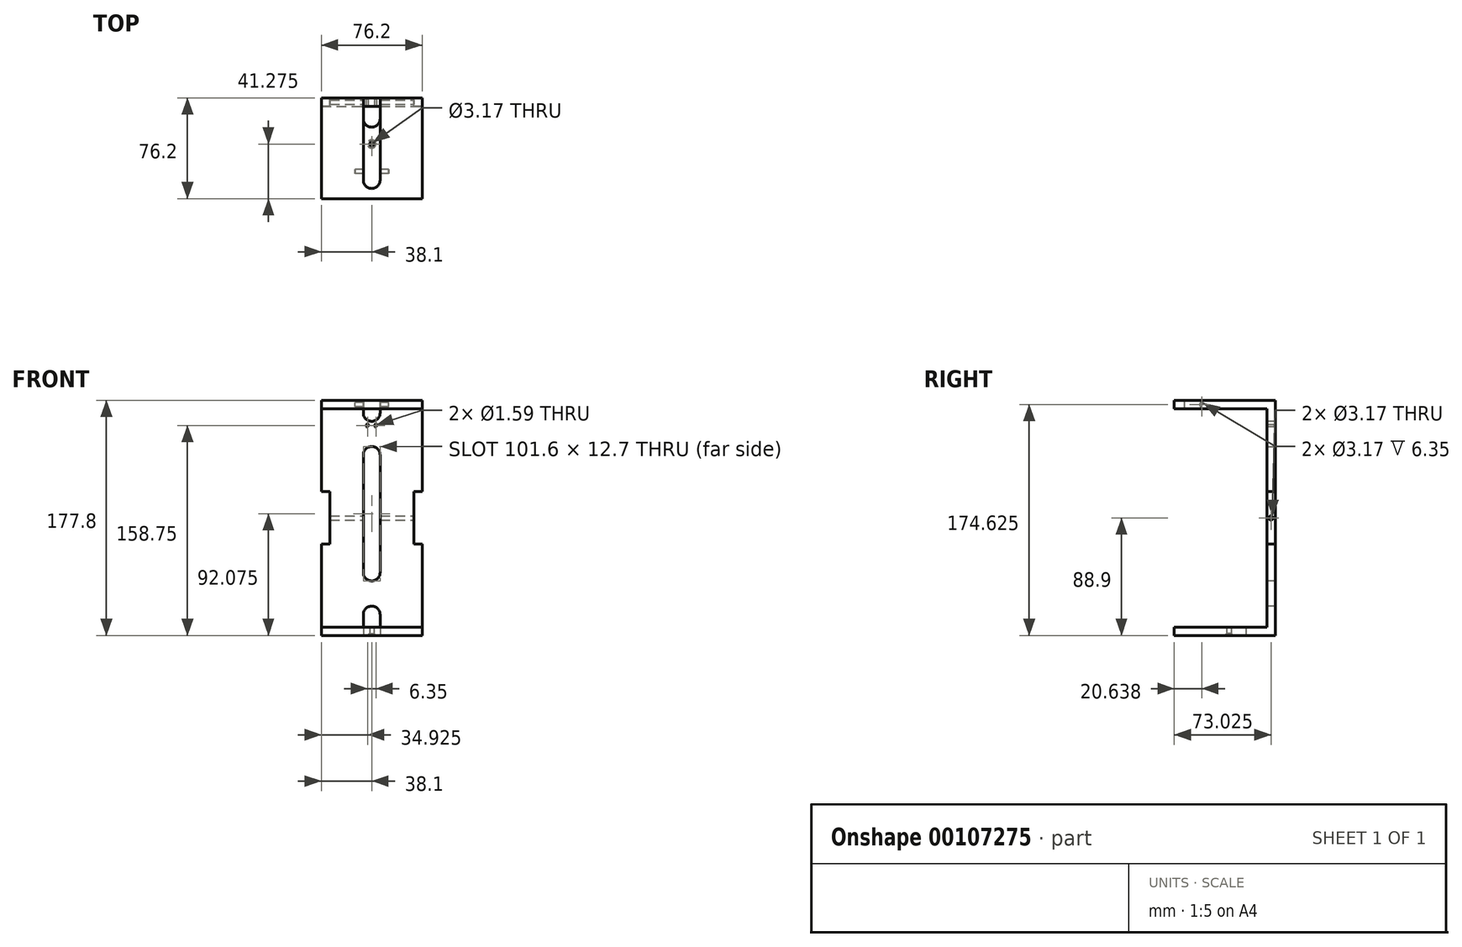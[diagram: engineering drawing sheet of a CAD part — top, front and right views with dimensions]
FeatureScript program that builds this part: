
annotation { "Feature Type Name" : "Feature", "Feature Type Description" : "" }
export const myFeature = defineFeature(function(context is Context, id is Id, definition is map)
    precondition{}
    {
        {
            var Q0;
            Q0=qCreatedBy(makeId("Front.planeOp"),FACE);
            var sketch = newSketch(context, id + "F0", { "sketchPlane" : qUnion([Q0])});
            skLineSegment(sketch, "E0.bottom", {"start": v(-38.1, 177.8) * mm, "end": v(38.1, 177.8) * mm});
            skLineSegment(sketch, "E0.top", {"start": v(-38.1, 0) * mm, "end": v(38.1, 0) * mm});
            skLineSegment(sketch, "E0.left", {"start": v(38.1, 177.8) * mm, "end": v(38.1, 0) * mm});
            skLineSegment(sketch, "E0.right", {"start": v(-38.1, 177.8) * mm, "end": v(-38.1, 0) * mm});
            skLineSegment(sketch, "E1", {"start": v(38.1, 171.45) * mm, "end": v(-38.1, 171.45) * mm});
            skLineSegment(sketch, "E2", {"start": v(38.1, 6.35) * mm, "end": v(-38.1, 6.35) * mm});
            skLineSegment(sketch, "E3.bottom", {"start": v(-6.35, 0) * mm, "end": v(6.35, 0) * mm});
            skLineSegment(sketch, "E3.top", {"start": v(-6.35, 22.22) * mm, "end": v(6.35, 22.23) * mm});
            skLineSegment(sketch, "E3.left", {"start": v(-6.35, 0) * mm, "end": v(-6.35, 22.22) * mm});
            skLineSegment(sketch, "E3.right", {"start": v(6.35, 0) * mm, "end": v(6.35, 22.22) * mm});
            skLineSegment(sketch, "E4.bottom", {"start": v(-6.35, 177.8) * mm, "end": v(6.35, 177.8) * mm});
            skLineSegment(sketch, "E4.top", {"start": v(-6.35, 161.92) * mm, "end": v(6.35, 161.92) * mm});
            skLineSegment(sketch, "E4.left", {"start": v(-6.35, 177.8) * mm, "end": v(-6.35, 161.92) * mm});
            skLineSegment(sketch, "E4.right", {"start": v(6.35, 177.8) * mm, "end": v(6.35, 161.92) * mm});
            skLineSegment(sketch, "E5.bottom", {"start": v(-6.35, 142.87) * mm, "end": v(6.35, 142.87) * mm});
            skLineSegment(sketch, "E5.top", {"start": v(-6.35, 41.28) * mm, "end": v(6.35, 41.28) * mm});
            skLineSegment(sketch, "E5.left", {"start": v(-6.35, 142.87) * mm, "end": v(-6.35, 41.28) * mm});
            skLineSegment(sketch, "E5.right", {"start": v(6.35, 142.87) * mm, "end": v(6.35, 41.28) * mm});
            skPoint(sketch, "E6", {"position": v(3.17, 158.75) * mm});
            skPoint(sketch, "E7", {"position": v(-3.17, 158.75) * mm});
            skLineSegment(sketch, "E8.bottom", {"start": v(38.1, 108.71) * mm, "end": v(31.75, 108.71) * mm});
            skLineSegment(sketch, "E8.top", {"start": v(38.1, 69.09) * mm, "end": v(31.75, 69.09) * mm});
            skLineSegment(sketch, "E8.left", {"start": v(38.1, 108.71) * mm, "end": v(38.1, 69.09) * mm});
            skLineSegment(sketch, "E8.right", {"start": v(31.75, 108.71) * mm, "end": v(31.75, 69.09) * mm});
            skLineSegment(sketch, "E9.bottom", {"start": v(-31.75, 108.71) * mm, "end": v(-38.1, 108.71) * mm});
            skLineSegment(sketch, "E9.top", {"start": v(-31.75, 69.09) * mm, "end": v(-38.1, 69.09) * mm});
            skLineSegment(sketch, "E9.left", {"start": v(-31.75, 108.71) * mm, "end": v(-31.75, 69.09) * mm});
            skLineSegment(sketch, "E9.right", {"start": v(-38.1, 108.71) * mm, "end": v(-38.1, 69.09) * mm});
            skSolve(sketch);
        }
        {
            var Q0;
            {var subQ0=sQuery(id+"F0.wireOp",EDGE,"E0.bottom");Q0=makeQuery(id+"F0.imprint","IMPRINT",FACE,{"disambiguationData":[TD([[makeQuery(id+"F0.imprint","IMPRINT",EDGE,{"derivedFrom":subQ0}),-1.0]])]});}
            var Q1;
            {var subQ0=sQuery(id+"F0.wireOp",EDGE,"E0.top");Q1=makeQuery(id+"F0.imprint","IMPRINT",FACE,{"disambiguationData":[TD([[makeQuery(id+"F0.imprint","IMPRINT",EDGE,{"derivedFrom":subQ0}),1.0]])]});}
            var Q2;
            {var subQ0=sQuery(id+"F0.wireOp",EDGE,"E1");Q2=makeQuery(id+"F0.imprint","IMPRINT",FACE,{"disambiguationData":[TD([[makeQuery(id+"F0.imprint","IMPRINT",EDGE,{"derivedFrom":subQ0}),1.0]])]});}
            extrude(context, id + "F1", {"entities" : qUnion([Q0, Q1, Q2]), "depth" : 6.35 * mm});
        }
        {
            var Q0;
            {var subQ0=sQuery(id+"F0.wireOp",EDGE,"E0.bottom");Q0=makeQuery(id+"F0.imprint","IMPRINT",FACE,{"disambiguationData":[TD([[makeQuery(id+"F0.imprint","IMPRINT",EDGE,{"derivedFrom":subQ0}),-1.0]])]});}
            var Q1;
            {var subQ0=sQuery(id+"F0.wireOp",EDGE,"E0.top");Q1=makeQuery(id+"F0.imprint","IMPRINT",FACE,{"disambiguationData":[TD([[makeQuery(id+"F0.imprint","IMPRINT",EDGE,{"derivedFrom":subQ0}),1.0]])]});}
            var Q2;
            {var subQ5=sQuery(id+"F0.wireOp",EDGE,"E3.bottom");Q2=makeQuery(id+"F0.imprint","IMPRINT",FACE,{"disambiguationData":[TD([[makeQuery(id+"F0.imprint","IMPRINT",EDGE,{"derivedFrom":subQ5}),1.0]])]});}
            var Q3;
            {var subQ5=sQuery(id+"F0.wireOp",EDGE,"E4.bottom");Q3=makeQuery(id+"F0.imprint","IMPRINT",FACE,{"disambiguationData":[TD([[makeQuery(id+"F0.imprint","IMPRINT",EDGE,{"derivedFrom":subQ5}),-1.0]])]});}
            extrude(context, id + "F2", {"entities" : qUnion([Q0, Q1, Q2, Q3]), "operationType" : NewBodyOperationType.ADD, "depth" : 76.2 * mm});
        }
        {
            var Q0;
            {var subQ0=sQuery(id+"F0.wireOp",EDGE,"E4.bottom");var subQ1=sQuery(id+"F0.wireOp",EDGE,"E0.bottom");Q0=makeQuery(id+"F2.boolean.opBoolean","MERGE",FACE,{"derivedFrom":[makeQuery(id+"F1.opExtrude","SWEPT_FACE",FACE,{"disambiguationData":[OSD([subQ1]),TDD([makeQuery(id+"F0.imprint","IMPRINT",EDGE,{"disambiguationData":[TD([[makeQuery(id+"F0.imprint","INTERSECT",VERTEX,{"derivedFrom":[subQ1,sQuery(id+"F0.wireOp",EDGE,"E0.right")]}),-1.0]])],"derivedFrom":subQ1})])]}),makeQuery(id+"F1.opExtrude","SWEPT_FACE",FACE,{"disambiguationData":[OSD([subQ1]),TDD([makeQuery(id+"F0.imprint","IMPRINT",EDGE,{"disambiguationData":[TD([[makeQuery(id+"F0.imprint","INTERSECT",VERTEX,{"derivedFrom":[subQ1,sQuery(id+"F0.wireOp",EDGE,"E0.left")]}),1.0]])],"derivedFrom":subQ1})])]}),makeQuery(id+"F2.opExtrude","SWEPT_FACE",FACE,{"disambiguationData":[OSD([subQ1,subQ0])]})]});}
            var sketch = newSketch(context, id + "F3", { "sketchPlane" : qUnion([Q0])});
            skLineSegment(sketch, "E10.bottom", {"start": v(-6.35, 0) * mm, "end": v(6.35, 0) * mm});
            skLineSegment(sketch, "E10.top", {"start": v(-6.35, -68.58) * mm, "end": v(6.35, -68.58) * mm});
            skLineSegment(sketch, "E10.left", {"start": v(-6.35, 0) * mm, "end": v(-6.35, -68.58) * mm});
            skLineSegment(sketch, "E10.right", {"start": v(6.35, 0) * mm, "end": v(6.35, -68.58) * mm});
            skSolve(sketch);
        }
        {
            var Q0;
            Q0=makeQuery(id+"F3.imprint","IMPRINT",FACE,{"disambiguationData":[TD([[makeQuery(id+"F3.imprint","IMPRINT",EDGE,{"derivedFrom":sQuery(id+"F3.wireOp",EDGE,"E10.bottom")}),-1.0]])]});
            extrude(context, id + "F4", {"entities" : qUnion([Q0]), "operationType" : NewBodyOperationType.REMOVE, "endBound" : BoundingType.UP_TO_NEXT, "oppositeDirection" : true, "depth" : 6.35 * mm});
        }
        {
            var Q0;
            {var subQ0=sQuery(id+"F0.wireOp",EDGE,"E3.bottom");var subQ1=sQuery(id+"F0.wireOp",EDGE,"E0.top");Q0=makeQuery(id+"F2.boolean.opBoolean","MERGE",FACE,{"derivedFrom":[makeQuery(id+"F1.opExtrude","SWEPT_FACE",FACE,{"disambiguationData":[OSD([subQ1]),TDD([makeQuery(id+"F0.imprint","IMPRINT",EDGE,{"disambiguationData":[TD([[makeQuery(id+"F0.imprint","INTERSECT",VERTEX,{"derivedFrom":[subQ1,sQuery(id+"F0.wireOp",EDGE,"E0.right")]}),-1.0]])],"derivedFrom":subQ1})])]}),makeQuery(id+"F1.opExtrude","SWEPT_FACE",FACE,{"disambiguationData":[OSD([subQ1]),TDD([makeQuery(id+"F0.imprint","IMPRINT",EDGE,{"disambiguationData":[TD([[makeQuery(id+"F0.imprint","INTERSECT",VERTEX,{"derivedFrom":[subQ1,sQuery(id+"F0.wireOp",EDGE,"E0.left")]}),1.0]])],"derivedFrom":subQ1})])]}),makeQuery(id+"F2.opExtrude","SWEPT_FACE",FACE,{"disambiguationData":[OSD([subQ1,subQ0])]})]});}
            var sketch = newSketch(context, id + "F5", { "sketchPlane" : qUnion([Q0])});
            skLineSegment(sketch, "E11.bottom", {"start": v(6.35, 22.22) * mm, "end": v(-6.35, 22.22) * mm});
            skLineSegment(sketch, "E11.top", {"start": v(6.35, 0) * mm, "end": v(-6.35, 0) * mm});
            skLineSegment(sketch, "E11.left", {"start": v(-6.35, 22.22) * mm, "end": v(-6.35, 0) * mm});
            skLineSegment(sketch, "E11.right", {"start": v(6.35, 22.22) * mm, "end": v(6.35, 0) * mm});
            skSolve(sketch);
        }
        {
            var Q0;
            Q0=qSketchRegion(id+"F5",true);
            extrude(context, id + "F6", {"entities" : qUnion([Q0]), "operationType" : NewBodyOperationType.REMOVE, "endBound" : BoundingType.UP_TO_NEXT, "oppositeDirection" : true, "depth" : 25.4 * mm});
        }
        {
            var Q0;
            Q0=sQuery(id+"F0.wireOp",VERTEX,"E7");
            var Q1;
            Q1=sQuery(id+"F0.wireOp",VERTEX,"E6");
            var Q2;
            Q2=makeQuery(id+"F1.opExtrude","SWEPT_BODY",BODY,{"disambiguationData":[OSD([sQuery(id+"F0.wireOp",EDGE,"E0.bottom"),sQuery(id+"F0.wireOp",EDGE,"E0.top"),sQuery(id+"F0.wireOp",EDGE,"E0.left"),sQuery(id+"F0.wireOp",EDGE,"E0.right"),sQuery(id+"F0.wireOp",EDGE,"E3.top"),sQuery(id+"F0.wireOp",EDGE,"E3.left"),sQuery(id+"F0.wireOp",EDGE,"E3.right"),sQuery(id+"F0.wireOp",EDGE,"E4.top"),sQuery(id+"F0.wireOp",EDGE,"E4.left"),sQuery(id+"F0.wireOp",EDGE,"E4.right"),sQuery(id+"F0.wireOp",EDGE,"E5.bottom"),sQuery(id+"F0.wireOp",EDGE,"E5.top"),sQuery(id+"F0.wireOp",EDGE,"E5.left"),sQuery(id+"F0.wireOp",EDGE,"E5.right")])]});
            hole(context, id + "F7", {"style" : HoleStyle.C_SINK, "endStyle" : HoleEndStyle.THROUGH, "oppositeDirection" : true, "holeDiameter" : 1.59 * mm, "cSinkDiameter" : 3.17 * mm, "cSinkAngle" : 90 * degree, "locations" : qUnion([Q0, Q1]), "scope" : qUnion([Q2]), "isTappedThrough" : true});
        }
        {
            var Q0;
            Q0=makeQuery(id+"F1.opExtrude","SWEPT_EDGE",EDGE,{"disambiguationData":[OSD([sQuery(id+"F0.wireOp",EDGE,"E3.top"),sQuery(id+"F0.wireOp",EDGE,"E3.left")])]});
            var Q1;
            Q1=makeQuery(id+"F1.opExtrude","SWEPT_EDGE",EDGE,{"disambiguationData":[OSD([sQuery(id+"F0.wireOp",EDGE,"E3.top"),sQuery(id+"F0.wireOp",EDGE,"E3.right")])]});
            var Q2;
            Q2=makeQuery(id+"F1.opExtrude","SWEPT_EDGE",EDGE,{"disambiguationData":[OSD([sQuery(id+"F0.wireOp",EDGE,"E4.top"),sQuery(id+"F0.wireOp",EDGE,"E4.left")])]});
            var Q3;
            Q3=makeQuery(id+"F1.opExtrude","SWEPT_EDGE",EDGE,{"disambiguationData":[OSD([sQuery(id+"F0.wireOp",EDGE,"E4.top"),sQuery(id+"F0.wireOp",EDGE,"E4.right")])]});
            var Q4;
            Q4=makeQuery(id+"F4.boolean.opBoolean","COPY",EDGE,{"derivedFrom":makeQuery(id+"F4.opExtrude","SWEPT_EDGE",EDGE,{"disambiguationData":[OSD([sQuery(id+"F3.wireOp",EDGE,"E10.top"),sQuery(id+"F3.wireOp",EDGE,"E10.left")])]})});
            var Q5;
            Q5=makeQuery(id+"F4.boolean.opBoolean","COPY",EDGE,{"derivedFrom":makeQuery(id+"F4.opExtrude","SWEPT_EDGE",EDGE,{"disambiguationData":[OSD([sQuery(id+"F3.wireOp",EDGE,"E10.top"),sQuery(id+"F3.wireOp",EDGE,"E10.right")])]})});
            var Q6;
            Q6=makeQuery(id+"F6.boolean.opBoolean","COPY",EDGE,{"derivedFrom":makeQuery(id+"F6.opExtrude","SWEPT_EDGE",EDGE,{"disambiguationData":[OSD([sQuery(id+"F5.wireOp",EDGE,"E11.bottom"),sQuery(id+"F5.wireOp",EDGE,"E11.right")])]})});
            var Q7;
            Q7=makeQuery(id+"F6.boolean.opBoolean","COPY",EDGE,{"derivedFrom":makeQuery(id+"F6.opExtrude","SWEPT_EDGE",EDGE,{"disambiguationData":[OSD([sQuery(id+"F5.wireOp",EDGE,"E11.bottom"),sQuery(id+"F5.wireOp",EDGE,"E11.left")])]})});
            var Q8;
            Q8=makeQuery(id+"F1.opExtrude","SWEPT_EDGE",EDGE,{"disambiguationData":[OSD([sQuery(id+"F0.wireOp",EDGE,"E5.top"),sQuery(id+"F0.wireOp",EDGE,"E5.left")])]});
            var Q9;
            Q9=makeQuery(id+"F1.opExtrude","SWEPT_EDGE",EDGE,{"disambiguationData":[OSD([sQuery(id+"F0.wireOp",EDGE,"E5.top"),sQuery(id+"F0.wireOp",EDGE,"E5.right")])]});
            var Q10;
            Q10=makeQuery(id+"F1.opExtrude","SWEPT_EDGE",EDGE,{"disambiguationData":[OSD([sQuery(id+"F0.wireOp",EDGE,"E5.bottom"),sQuery(id+"F0.wireOp",EDGE,"E5.left")])]});
            var Q11;
            Q11=makeQuery(id+"F1.opExtrude","SWEPT_EDGE",EDGE,{"disambiguationData":[OSD([sQuery(id+"F0.wireOp",EDGE,"E5.bottom"),sQuery(id+"F0.wireOp",EDGE,"E5.right")])]});
            fillet(context, id + "F8", {"entities" : qUnion([Q0, Q1, Q2, Q3, Q4, Q5, Q6, Q7, Q8, Q9, Q10, Q11]), "radius" : 6.35 * mm, "tangentPropagation" : true, "allowEdgeOverflow" : false});
        }
        {
            var Q0;
            {var subQ0=sQuery(id+"F0.wireOp",EDGE,"E0.left");Q0=makeQuery(id+"F2.boolean.opBoolean","MERGE",FACE,{"derivedFrom":[makeQuery(id+"F1.opExtrude","SWEPT_FACE",FACE,{"disambiguationData":[OSD([subQ0])]}),makeQuery(id+"F2.opExtrude","SWEPT_FACE",FACE,{"disambiguationData":[OSD([subQ0]),TDD([makeQuery(id+"F0.imprint","IMPRINT",EDGE,{"disambiguationData":[TD([[makeQuery(id+"F0.imprint","INTERSECT",VERTEX,{"derivedFrom":[sQuery(id+"F0.wireOp",EDGE,"E0.bottom"),subQ0]}),-1.0]])],"derivedFrom":subQ0})])]}),makeQuery(id+"F2.opExtrude","SWEPT_FACE",FACE,{"disambiguationData":[OSD([subQ0]),TDD([makeQuery(id+"F0.imprint","IMPRINT",EDGE,{"disambiguationData":[TD([[makeQuery(id+"F0.imprint","INTERSECT",VERTEX,{"derivedFrom":[sQuery(id+"F0.wireOp",EDGE,"E0.top"),subQ0]}),1.0]])],"derivedFrom":subQ0})])]})]});}
            var sketch = newSketch(context, id + "F9", { "sketchPlane" : qUnion([Q0])});
            skPoint(sketch, "E12", {"position": v(-3.18, 88.9) * mm});
            skSolve(sketch);
        }
        {
            var Q0;
            Q0=sQuery(id+"F9.wireOp",VERTEX,"E12");
            var Q1;
            Q1=makeQuery(id+"F1.opExtrude","SWEPT_BODY",BODY,{"disambiguationData":[OSD([sQuery(id+"F0.wireOp",EDGE,"E0.bottom"),sQuery(id+"F0.wireOp",EDGE,"E0.top"),sQuery(id+"F0.wireOp",EDGE,"E0.left"),sQuery(id+"F0.wireOp",EDGE,"E0.right"),sQuery(id+"F0.wireOp",EDGE,"E3.top"),sQuery(id+"F0.wireOp",EDGE,"E3.left"),sQuery(id+"F0.wireOp",EDGE,"E3.right"),sQuery(id+"F0.wireOp",EDGE,"E4.top"),sQuery(id+"F0.wireOp",EDGE,"E4.left"),sQuery(id+"F0.wireOp",EDGE,"E4.right"),sQuery(id+"F0.wireOp",EDGE,"E5.bottom"),sQuery(id+"F0.wireOp",EDGE,"E5.top"),sQuery(id+"F0.wireOp",EDGE,"E5.left"),sQuery(id+"F0.wireOp",EDGE,"E5.right")])]});
            hole(context, id + "F10", {"style" : HoleStyle.SIMPLE, "endStyle" : HoleEndStyle.THROUGH, "holeDiameter" : 3.17 * mm, "locations" : qUnion([Q0]), "scope" : qUnion([Q1]), "isTappedThrough" : true});
        }
        {
            var Q0;
            {var subQ0=sQuery(id+"F0.wireOp",EDGE,"E3.bottom");var subQ1=sQuery(id+"F0.wireOp",EDGE,"E0.top");Q0=makeQuery(id+"F2.boolean.opBoolean","MERGE",FACE,{"derivedFrom":[makeQuery(id+"F1.opExtrude","SWEPT_FACE",FACE,{"disambiguationData":[OSD([subQ1]),TDD([makeQuery(id+"F0.imprint","IMPRINT",EDGE,{"disambiguationData":[TD([[makeQuery(id+"F0.imprint","INTERSECT",VERTEX,{"derivedFrom":[subQ1,sQuery(id+"F0.wireOp",EDGE,"E0.right")]}),-1.0]])],"derivedFrom":subQ1})])]}),makeQuery(id+"F1.opExtrude","SWEPT_FACE",FACE,{"disambiguationData":[OSD([subQ1]),TDD([makeQuery(id+"F0.imprint","IMPRINT",EDGE,{"disambiguationData":[TD([[makeQuery(id+"F0.imprint","INTERSECT",VERTEX,{"derivedFrom":[subQ1,sQuery(id+"F0.wireOp",EDGE,"E0.left")]}),1.0]])],"derivedFrom":subQ1})])]}),makeQuery(id+"F2.opExtrude","SWEPT_FACE",FACE,{"disambiguationData":[OSD([subQ1,subQ0])]})]});}
            var sketch = newSketch(context, id + "F11", { "sketchPlane" : qUnion([Q0])});
            skPoint(sketch, "E13", {"position": v(0, 34.92) * mm});
            skSolve(sketch);
        }
        {
            var Q0;
            Q0=sQuery(id+"F11.wireOp",VERTEX,"E13");
            var Q1;
            Q1=makeQuery(id+"F1.opExtrude","SWEPT_BODY",BODY,{"disambiguationData":[OSD([sQuery(id+"F0.wireOp",EDGE,"E0.bottom"),sQuery(id+"F0.wireOp",EDGE,"E0.top"),sQuery(id+"F0.wireOp",EDGE,"E0.left"),sQuery(id+"F0.wireOp",EDGE,"E0.right"),sQuery(id+"F0.wireOp",EDGE,"E3.top"),sQuery(id+"F0.wireOp",EDGE,"E3.left"),sQuery(id+"F0.wireOp",EDGE,"E3.right"),sQuery(id+"F0.wireOp",EDGE,"E4.top"),sQuery(id+"F0.wireOp",EDGE,"E4.left"),sQuery(id+"F0.wireOp",EDGE,"E4.right"),sQuery(id+"F0.wireOp",EDGE,"E5.bottom"),sQuery(id+"F0.wireOp",EDGE,"E5.top"),sQuery(id+"F0.wireOp",EDGE,"E5.left"),sQuery(id+"F0.wireOp",EDGE,"E5.right")])]});
            hole(context, id + "F12", {"style" : HoleStyle.C_SINK, "endStyle" : HoleEndStyle.THROUGH, "holeDiameter" : 3.17 * mm, "cSinkDiameter" : 6.35 * mm, "cSinkAngle" : 90 * degree, "locations" : qUnion([Q0]), "scope" : qUnion([Q1]), "isTappedThrough" : true});
        }
        {
            var Q0;
            Q0=qCreatedBy(makeId("Right.planeOp"),FACE);
            var sketch = newSketch(context, id + "F13", { "sketchPlane" : qUnion([Q0])});
            skCircle(sketch, "E14", {"center": v(-55.56, 174.62) * mm, "radius": 1.59 * mm});
            skSolve(sketch);
        }
        {
            var Q0;
            Q0=makeQuery(id+"F13.imprint","IMPRINT",FACE,{"disambiguationData":[TD([[makeQuery(id+"F13.imprint","IMPRINT",EDGE,{"derivedFrom":sQuery(id+"F13.wireOp",EDGE,"E14")}),1.0]])]});
            extrude(context, id + "F14", {"entities" : qUnion([Q0]), "operationType" : NewBodyOperationType.REMOVE, "endBound" : BoundingType.SYMMETRIC, "depth" : 25.4 * mm});
        }
    });
